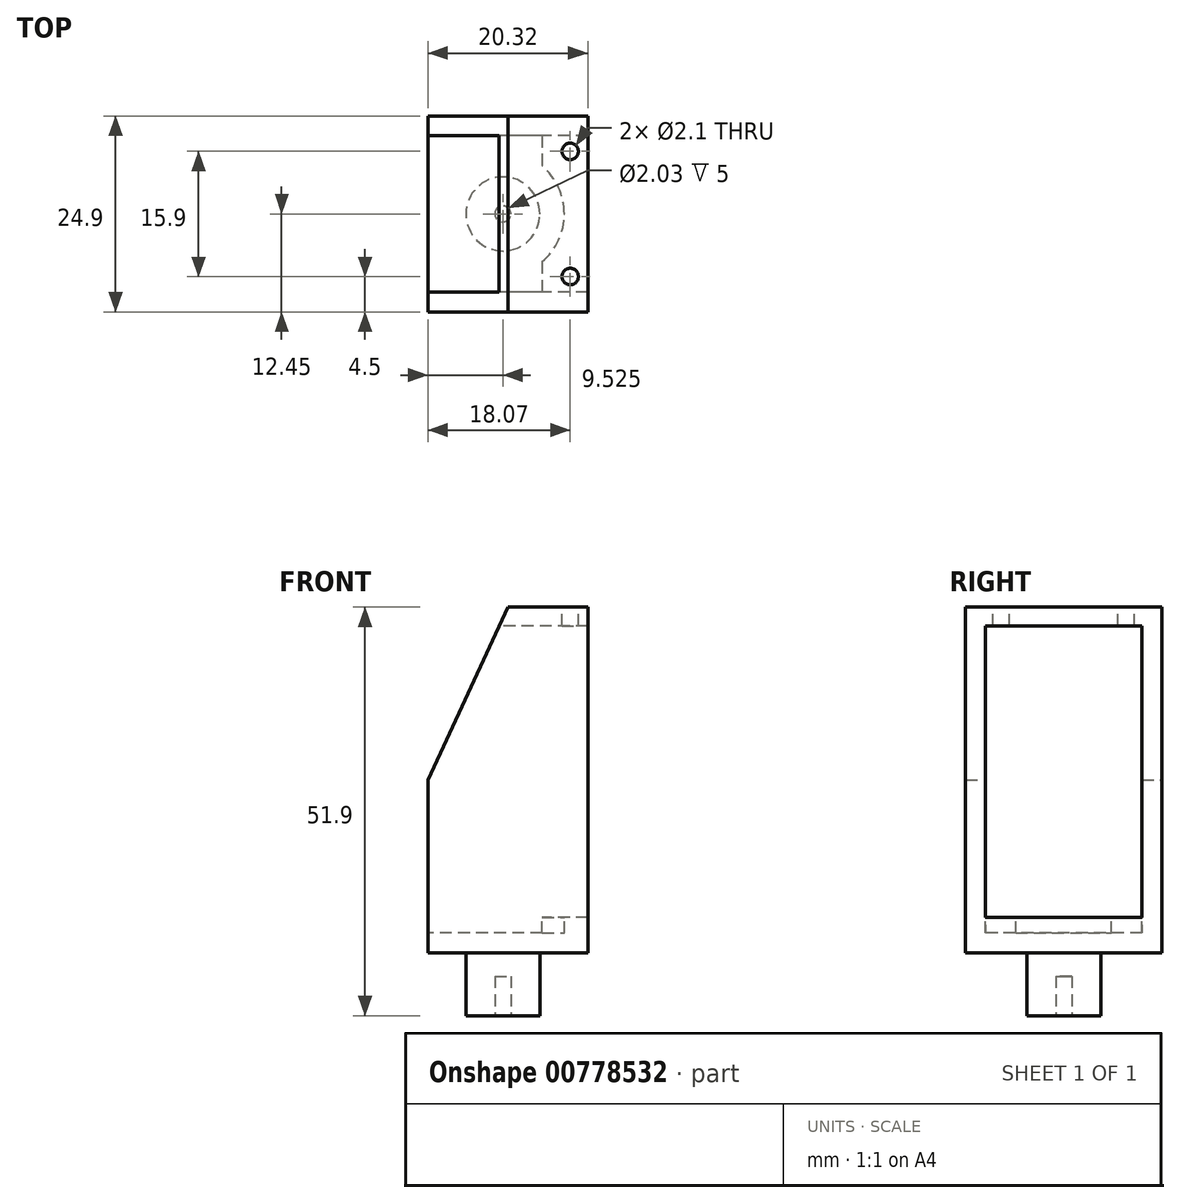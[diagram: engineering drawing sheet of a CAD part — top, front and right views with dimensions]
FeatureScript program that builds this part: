
annotation { "Feature Type Name" : "Feature", "Feature Type Description" : "" }
export const myFeature = defineFeature(function(context is Context, id is Id, definition is map)
    precondition{}
    {
        {
            var Q0;
            Q0=qCreatedBy(makeId("Front.planeOp"),FACE);
            var sketch = newSketch(context, id + "F0", { "sketchPlane" : qUnion([Q0])});
            skLineSegment(sketch, "E0.bottom", {"start": v(0, 21.95) * mm, "end": v(-10.16, 21.95) * mm});
            skLineSegment(sketch, "E0.top", {"start": v(10.16, -21.95) * mm, "end": v(-10.16, -21.95) * mm});
            skLineSegment(sketch, "E0.left", {"start": v(10.16, 0) * mm, "end": v(10.16, -21.95) * mm});
            skLineSegment(sketch, "E0.right", {"start": v(-10.16, 21.95) * mm, "end": v(-10.16, -21.95) * mm});
            skPoint(sketch, "E0.middle", {"position": v(0, 0) * mm});
            skPoint(sketch, "E1.orphan", {"position": v(10.16, 21.95) * mm});
            skLineSegment(sketch, "E2", {"start": v(0, 21.95) * mm, "end": v(10.16, 21.95) * mm});
            skLineSegment(sketch, "E3", {"start": v(10.16, 0) * mm, "end": v(10.16, 21.95) * mm});
            skSolve(sketch);
        }
        {
            var Q0;
            Q0=qSketchRegion(id+"F0",true);
            extrude(context, id + "F1", {"entities" : qUnion([Q0]), "depth" : 24.9 * mm, "offsetDistance" : 25.4 * mm});
        }
        {
            var Q0;
            Q0=makeQuery(id+"F1.opExtrude","SWEPT_FACE",FACE,{"disambiguationData":[OSD([sQuery(id+"F0.wireOp",EDGE,"E0.right")])]});
            var sketch = newSketch(context, id + "F2", { "sketchPlane" : qUnion([Q0])});
            skLineSegment(sketch, "E4.bottom", {"start": v(2.5, 19.55) * mm, "end": v(22.4, 19.55) * mm});
            skLineSegment(sketch, "E4.top", {"start": v(2.5, -16.95) * mm, "end": v(22.4, -16.95) * mm});
            skLineSegment(sketch, "E4.left", {"start": v(2.5, 19.55) * mm, "end": v(2.5, -16.95) * mm});
            skLineSegment(sketch, "E4.right", {"start": v(22.4, 19.55) * mm, "end": v(22.4, -16.95) * mm});
            skSolve(sketch);
        }
        {
            var Q0;
            Q0=qSketchRegion(id+"F2",true);
            extrude(context, id + "F3", {"entities" : qUnion([Q0]), "operationType" : NewBodyOperationType.REMOVE, "oppositeDirection" : true, "depth" : 25.4 * mm, "offsetDistance" : 25.4 * mm});
        }
        {
            var Q0;
            Q0=makeQuery(id+"F1.opExtrude","SWEPT_FACE",FACE,{"disambiguationData":[OSD([sQuery(id+"F0.wireOp",EDGE,"E0.right")])]});
            var sketch = newSketch(context, id + "F4", { "sketchPlane" : qUnion([Q0])});
            skLineSegment(sketch, "E5.bottom", {"start": v(0, 21.95) * mm, "end": v(24.9, 21.95) * mm});
            skLineSegment(sketch, "E5.top", {"start": v(0, 16.95) * mm, "end": v(24.9, 16.95) * mm});
            skLineSegment(sketch, "E5.left", {"start": v(0, 21.95) * mm, "end": v(0, 16.95) * mm});
            skLineSegment(sketch, "E5.right", {"start": v(24.9, 21.95) * mm, "end": v(24.9, 16.95) * mm});
            skLineSegment(sketch, "E6.bottom", {"start": v(0, -21.95) * mm, "end": v(24.9, -21.95) * mm});
            skLineSegment(sketch, "E6.top", {"start": v(0, -14.45) * mm, "end": v(24.9, -14.45) * mm});
            skLineSegment(sketch, "E6.left", {"start": v(0, -21.95) * mm, "end": v(0, -14.45) * mm});
            skLineSegment(sketch, "E6.right", {"start": v(24.9, -21.95) * mm, "end": v(24.9, -14.45) * mm});
            skSolve(sketch);
        }
        {
            var Q0;
            Q0=qSketchRegion(id+"F4",true);
            extrude(context, id + "F5", {"entities" : qUnion([Q0]), "operationType" : NewBodyOperationType.ADD, "depth" : 2.5 * mm, "offsetDistance" : 25.4 * mm});
        }
        {
            var Q0;
            Q0=makeQuery(id+"F3.boolean.opBoolean","COPY",FACE,{"derivedFrom":makeQuery(id+"F3.opExtrude","SWEPT_FACE",FACE,{"disambiguationData":[OSD([sQuery(id+"F2.wireOp",EDGE,"E4.top")])]})});
            var sketch = newSketch(context, id + "F6", { "sketchPlane" : qUnion([Q0])});
            skLineSegment(sketch, "E7.bottom", {"start": v(10.16, -2.5) * mm, "end": v(4.36, -2.5) * mm});
            skLineSegment(sketch, "E7.top", {"start": v(10.16, -22.4) * mm, "end": v(4.36, -22.4) * mm});
            skLineSegment(sketch, "E7.left", {"start": v(10.16, -2.5) * mm, "end": v(10.16, -22.4) * mm});
            skLineSegment(sketch, "E7.right", {"start": v(4.36, -2.5) * mm, "end": v(4.36, -6.37) * mm});
            skPoint(sketch, "E8", {"position": v(-0.84, -12.45) * mm});
            skPoint(sketch, "E8.positionSnap0", {"position": v(4.36, -12.45) * mm});
            skArc(sketch, "E9", {"start": v(4.36, -6.37) * mm, "mid": v(7.16, -12.45) * mm, "end": v(4.36, -18.53) * mm});
            skLineSegment(sketch, "E10.trimOffspring", {"start": v(4.36, -18.53) * mm, "end": v(4.36, -22.4) * mm});
            skSolve(sketch);
        }
        {
            var Q0;
            {var subQ3=sQuery(id+"F6.wireOp",EDGE,"E7.right");Q0=makeQuery(id+"F6.imprint","IMPRINT",FACE,{"disambiguationData":[TD([[makeQuery(id+"F6.imprint","IMPRINT",EDGE,{"derivedFrom":subQ3}),-1.0]])]});}
            extrude(context, id + "F7", {"entities" : qUnion([Q0]), "operationType" : NewBodyOperationType.REMOVE, "oppositeDirection" : true, "depth" : 2.5 * mm, "offsetDistance" : 25.4 * mm});
        }
        {
            var Q0;
            Q0=makeQuery(id+"F5.boolean.opBoolean","MERGE",FACE,{"derivedFrom":[makeQuery(id+"F1.opExtrude","SWEPT_FACE",FACE,{"disambiguationData":[OSD([sQuery(id+"F0.wireOp",EDGE,"E0.bottom")])]}),makeQuery(id+"F5.opExtrude","SWEPT_FACE",FACE,{"disambiguationData":[OSD([sQuery(id+"F4.wireOp",EDGE,"E5.bottom")])]})]});
            var sketch = newSketch(context, id + "F8", { "sketchPlane" : qUnion([Q0])});
            skLineSegment(sketch, "E11", {"start": v(-31.79, -12.45) * mm, "end": v(21.26, -12.45) * mm, "construction": true});
            skPoint(sketch, "E11.startSnap0", {"position": v(-12.66, -12.45) * mm});
            skLineSegment(sketch, "E12", {"start": v(0, 0) * mm, "end": v(0, -24.9) * mm, "construction": true});
            skCircle(sketch, "E13.MirrorC", {"center": v(7.9, -4.5) * mm, "radius": 1.05 * mm});
            skCircle(sketch, "E14.MirrorC", {"center": v(7.9, -20.4) * mm, "radius": 1.05 * mm});
            skPoint(sketch, "E15.center.orphan", {"position": v(-7.9, -4.5) * mm});
            skSolve(sketch);
        }
        {
            var Q0;
            Q0=qSketchRegion(id+"F8",true);
            extrude(context, id + "F9", {"entities" : qUnion([Q0]), "operationType" : NewBodyOperationType.REMOVE, "oppositeDirection" : true, "depth" : 25.4 * mm, "offsetDistance" : 25.4 * mm});
        }
        {
            var Q0;
            Q0=makeQuery(id+"F5.boolean.opBoolean","MERGE",FACE,{"derivedFrom":[makeQuery(id+"F1.opExtrude","SWEPT_FACE",FACE,{"disambiguationData":[OSD([sQuery(id+"F0.wireOp",EDGE,"E0.top")])]}),makeQuery(id+"F5.opExtrude","SWEPT_FACE",FACE,{"disambiguationData":[OSD([sQuery(id+"F4.wireOp",EDGE,"E6.bottom")])]})]});
            var sketch = newSketch(context, id + "F10", { "sketchPlane" : qUnion([Q0])});
            skCircle(sketch, "E16", {"center": v(-0.64, 12.45) * mm, "radius": 4.7 * mm});
            skLineSegment(sketch, "E17", {"start": v(-12.66, 12.45) * mm, "end": v(10.16, 12.45) * mm, "construction": true});
            skSolve(sketch);
        }
        {
            var Q0;
            Q0=qSketchRegion(id+"F10",true);
            extrude(context, id + "F11", {"entities" : qUnion([Q0]), "operationType" : NewBodyOperationType.ADD, "depth" : 8 * mm, "offsetDistance" : 25.4 * mm});
        }
        {
            var Q0;
            Q0=makeQuery(id+"F11.opExtrude","CAP_FACE",FACE,{"disambiguationData":[OSD([sQuery(id+"F10.wireOp",EDGE,"E16")])],"isStart":false});
            var sketch = newSketch(context, id + "F12", { "sketchPlane" : qUnion([Q0])});
            skCircle(sketch, "E18", {"center": v(-0.64, 12.45) * mm, "radius": 1.02 * mm});
            skSolve(sketch);
        }
        {
            var Q0;
            Q0=qSketchRegion(id+"F12",true);
            extrude(context, id + "F13", {"entities" : qUnion([Q0]), "operationType" : NewBodyOperationType.REMOVE, "oppositeDirection" : true, "depth" : 5 * mm, "offsetDistance" : 25.4 * mm});
        }
        {
            var Q0;
            Q0=makeQuery(id+"F5.boolean.opBoolean","MERGE",FACE,{"derivedFrom":[makeQuery(id+"F1.opExtrude","CAP_FACE",FACE,{"disambiguationData":[OSD([sQuery(id+"F0.wireOp",EDGE,"E0.bottom"),sQuery(id+"F0.wireOp",EDGE,"E0.top"),sQuery(id+"F0.wireOp",EDGE,"E0.left"),sQuery(id+"F0.wireOp",EDGE,"E0.right"),sQuery(id+"F0.wireOp",EDGE,"q2moGxQV-aD0Y-tgfn-xWST-8mHXIR3H3rI7")])],"isStart":false}),makeQuery(id+"F5.opExtrude","SWEPT_FACE",FACE,{"disambiguationData":[OSD([sQuery(id+"F4.wireOp",EDGE,"E5.right")])]}),makeQuery(id+"F5.opExtrude","SWEPT_FACE",FACE,{"disambiguationData":[OSD([sQuery(id+"F4.wireOp",EDGE,"E6.right")])]})]});
            var sketch = newSketch(context, id + "F14", { "sketchPlane" : qUnion([Q0])});
            skLineSegment(sketch, "E19.bottom", {"start": v(-12.66, -14.45) * mm, "end": v(-10.16, -14.45) * mm});
            skLineSegment(sketch, "E19.top", {"start": v(-12.66, -21.95) * mm, "end": v(-10.16, -21.95) * mm});
            skLineSegment(sketch, "E19.left", {"start": v(-12.66, -14.45) * mm, "end": v(-12.66, -21.95) * mm});
            skLineSegment(sketch, "E19.right", {"start": v(-10.16, -14.45) * mm, "end": v(-10.16, -21.95) * mm});
            skLineSegment(sketch, "E20.bottom", {"start": v(-12.66, 16.95) * mm, "end": v(-10.16, 16.95) * mm});
            skLineSegment(sketch, "E20.top", {"start": v(-12.66, 21.95) * mm, "end": v(-10.16, 21.95) * mm});
            skLineSegment(sketch, "E20.left", {"start": v(-12.66, 16.95) * mm, "end": v(-12.66, 21.95) * mm});
            skLineSegment(sketch, "E20.right", {"start": v(-10.16, 16.95) * mm, "end": v(-10.16, 21.95) * mm});
            skSolve(sketch);
        }
        {
            var Q0;
            Q0=qSketchRegion(id+"F14",true);
            extrude(context, id + "F15", {"entities" : qUnion([Q0]), "operationType" : NewBodyOperationType.REMOVE, "oppositeDirection" : true, "depth" : 25.4 * mm, "offsetDistance" : 25.4 * mm});
        }
        {
            var Q0;
            Q0=makeQuery(id+"F5.boolean.opBoolean","MERGE",FACE,{"derivedFrom":[makeQuery(id+"F1.opExtrude","CAP_FACE",FACE,{"disambiguationData":[OSD([sQuery(id+"F0.wireOp",EDGE,"E0.bottom"),sQuery(id+"F0.wireOp",EDGE,"E0.top"),sQuery(id+"F0.wireOp",EDGE,"E0.left"),sQuery(id+"F0.wireOp",EDGE,"E0.right"),sQuery(id+"F0.wireOp",EDGE,"E2"),sQuery(id+"F0.wireOp",EDGE,"E3")])],"isStart":true}),makeQuery(id+"F5.opExtrude","SWEPT_FACE",FACE,{"disambiguationData":[OSD([sQuery(id+"F4.wireOp",EDGE,"E5.left")])]}),makeQuery(id+"F5.opExtrude","SWEPT_FACE",FACE,{"disambiguationData":[OSD([sQuery(id+"F4.wireOp",EDGE,"E6.left")])]})]});
            var sketch = newSketch(context, id + "F16", { "sketchPlane" : qUnion([Q0])});
            skLineSegment(sketch, "E21", {"start": v(0, 21.95) * mm, "end": v(10.16, 0) * mm});
            skLineSegment(sketch, "E22", {"start": v(10.16, 0) * mm, "end": v(10.16, 21.95) * mm});
            skLineSegment(sketch, "E23", {"start": v(10.16, 21.95) * mm, "end": v(0, 21.95) * mm});
            skSolve(sketch);
        }
        {
            var Q0;
            Q0 = qSketchRegion(id + "F16", true);
            extrude(context, id + "F17", {"entities" : qUnion([Q0]), "operationType" : NewBodyOperationType.REMOVE, "oppositeDirection" : true, "depth" : 25.4 * mm, "offsetDistance" : 25.4 * mm});
        }
        {
            var Q0;
            Q0=makeQuery(id+"F3.boolean.opBoolean","COPY",FACE,{"derivedFrom":makeQuery(id+"F3.opExtrude","SWEPT_FACE",FACE,{"disambiguationData":[OSD([sQuery(id+"F2.wireOp",EDGE,"E4.top")])]})});
            var sketch = newSketch(context, id + "F18", { "sketchPlane" : qUnion([Q0])});
            skLineSegment(sketch, "E24.bottom", {"start": v(4.36, -22.4) * mm, "end": v(10.16, -22.4) * mm});
            skLineSegment(sketch, "E24.top", {"start": v(4.36, -2.5) * mm, "end": v(10.16, -2.5) * mm});
            skLineSegment(sketch, "E24.left", {"start": v(4.36, -22.4) * mm, "end": v(4.36, -2.5) * mm});
            skLineSegment(sketch, "E24.right", {"start": v(10.16, -22.4) * mm, "end": v(10.16, -2.5) * mm});
            skSolve(sketch);
        }
        {
            var Q0;
            Q0 = qSketchRegion(id + "F18", true);
            extrude(context, id + "F19", {"entities" : qUnion([Q0]), "operationType" : NewBodyOperationType.REMOVE, "oppositeDirection" : true, "depth" : 0.5 * mm, "offsetDistance" : 25.4 * mm});
        }
    });
